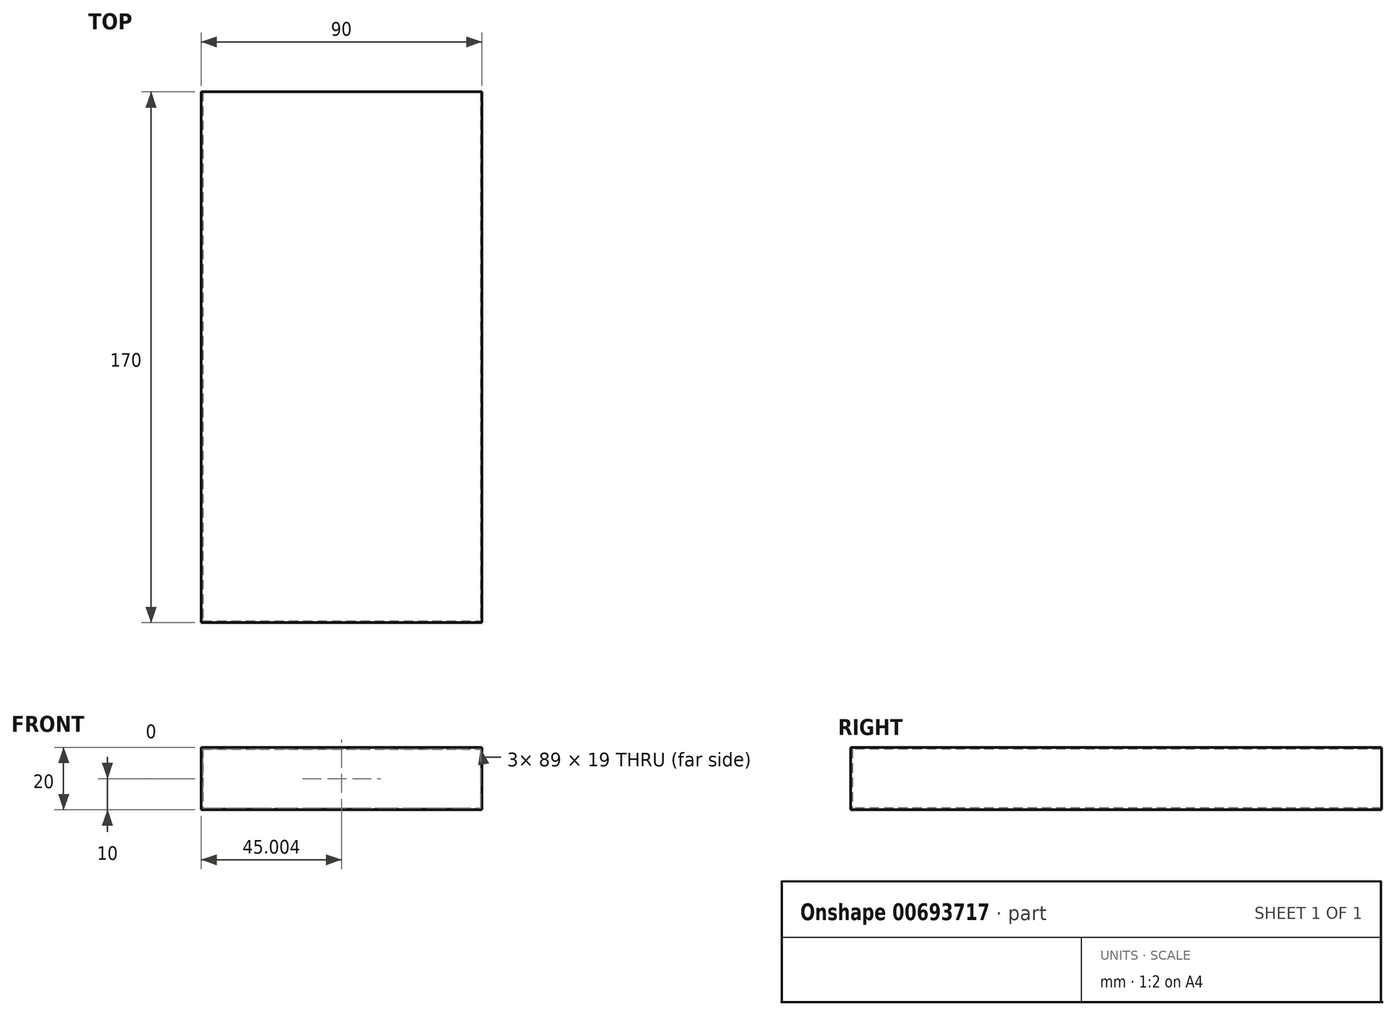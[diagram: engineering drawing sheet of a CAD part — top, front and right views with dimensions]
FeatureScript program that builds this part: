
annotation { "Feature Type Name" : "Feature", "Feature Type Description" : "" }
export const myFeature = defineFeature(function(context is Context, id is Id, definition is map)
    precondition{}
    {
        {
            var Q0;
            Q0=qCreatedBy(makeId("Top.planeOp"),FACE);
            var sketch = newSketch(context, id + "F0", { "sketchPlane" : qUnion([Q0])});
            skLineSegment(sketch, "E0.bottom", {"start": v(-64.7, 82.69) * mm, "end": v(25.3, 82.69) * mm});
            skLineSegment(sketch, "E0.top", {"start": v(-64.7, -87.31) * mm, "end": v(25.3, -87.31) * mm});
            skLineSegment(sketch, "E0.left", {"start": v(-64.7, 82.69) * mm, "end": v(-64.7, -87.31) * mm});
            skLineSegment(sketch, "E0.right", {"start": v(25.3, 82.69) * mm, "end": v(25.3, -87.31) * mm});
            skSolve(sketch);
        }
        {
            var Q0;
            Q0 = qSketchRegion(id + "F0", true);
            extrude(context, id + "F1", {"entities" : qUnion([Q0]), "depth" : 20 * mm, "offsetDistance" : 25 * mm});
        }
        {
            var Q0;
            Q0=makeQuery(id+"F1.opExtrude","SWEPT_FACE",FACE,{"disambiguationData":[OSD([sQuery(id+"F0.wireOp",EDGE,"E0.bottom")])]});
            shell(context, id + "F2", {"entities" : qUnion([Q0]), "thickness" : 0.5 * mm});
        }
    });
